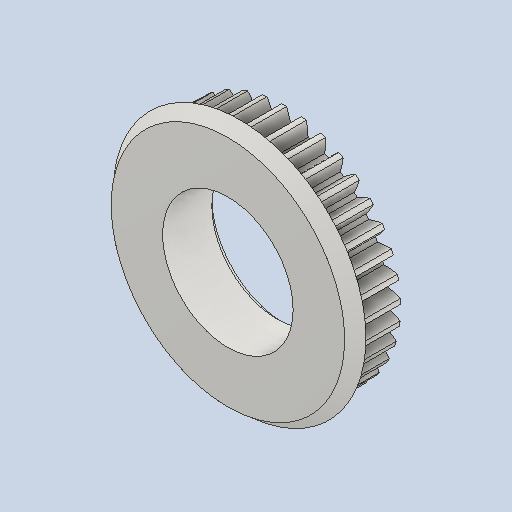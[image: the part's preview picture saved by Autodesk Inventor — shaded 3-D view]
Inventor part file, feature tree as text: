
AUTODESK INVENTOR PART (.ipt)
format: ipt  version: 2022 (Build 260153000, 153)  size: 1,216,512 bytes
history: native  units: mm (DEFAULTED — no unit token found)
features: sketch x4, plane x3, other x3, extrude x2, chamfer x1, revolve x1
ambient origin geometry x8: Origin, YZ Plane, XZ Plane, XY Plane, X Axis, Y Axis, Z Axis, Center Point
bodies: Solid1 (feature_tree)
feature tree (14):
  extrude  "Extrusion1"  Depth=9.525mm TaperAngle=0.0deg
  plane  "Work Plane1"
  plane  "Work Plane2"
  plane  "Work Plane3"
  other  "Spur Gear"
  extrude  "Extrusion2"  Depth=76.2mm TaperAngle=0.0deg
  chamfer  "Chamfer1"  Distance=0.849079mm
  revolve  "Revolution1"  [1 undecoded]
  sketch  "Sketch1"  dims[d0=39.506688mm d1=9.525mm d2=0.0mm]
  sketch  "Sketch2"  dims[d3=37.0mm d4=76.2mm d5=0.0mm d6=0.0mm d7=0.849079mm]
  other  "Srf1"
  sketch  "Sketch3"  dims[d9=0.0mm d14=0.0mm]
  sketch  "Sketch4"  dims[d15=23.753344mm d16=0.0mm d17=0.0mm d18=0.0mm d19=23.753344mm d20=22.1mm d21=0.0mm d22=0.0mm d23=1.2mm d24=3.175mm d25=45.0deg d26=35.0mm d27=6.35mm d30=3.175mm d31=19.75mm d32=360.0deg d33=22.68928mm d34=1.2mm]
  other  "Pitch Diameter"
note: 1 required parameter value undecoded (feature->parameter linkage not recoverable at this tier; creation-order binding heuristic only, values carry confidence <= 0.55)
